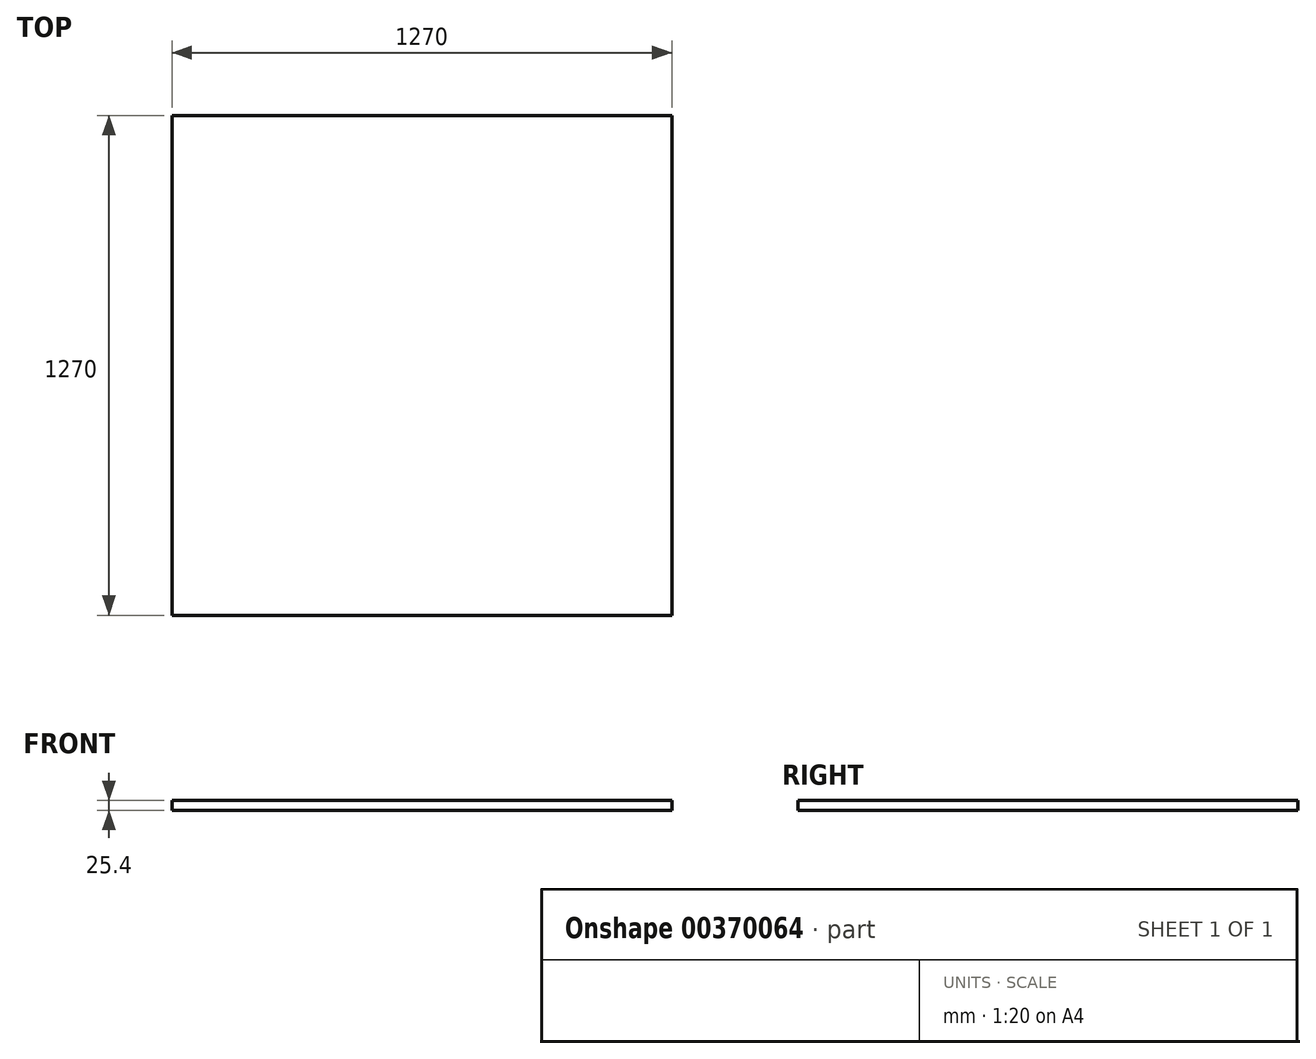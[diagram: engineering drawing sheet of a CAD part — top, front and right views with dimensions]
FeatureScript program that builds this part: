
annotation { "Feature Type Name" : "Feature", "Feature Type Description" : "" }
export const myFeature = defineFeature(function(context is Context, id is Id, definition is map)
    precondition{}
    {
        {
            var Q0;
            Q0=qCreatedBy(makeId("Top.planeOp"),FACE);
            var sketch = newSketch(context, id + "F0", { "sketchPlane" : qUnion([Q0])});
            skLineSegment(sketch, "E0.bottom", {"start": v(635, -302.65) * mm, "end": v(-635, -302.65) * mm});
            skLineSegment(sketch, "E0.top", {"start": v(635, 967.35) * mm, "end": v(-635, 967.35) * mm});
            skLineSegment(sketch, "E0.left", {"start": v(635, -302.65) * mm, "end": v(635, 967.35) * mm});
            skLineSegment(sketch, "E0.right", {"start": v(-635, -302.65) * mm, "end": v(-635, 967.35) * mm});
            skPoint(sketch, "E0.middle", {"position": v(0, 332.35) * mm});
            skLineSegment(sketch, "E1.bottom", {"start": v(-635, 256.77) * mm, "end": v(-635, 256.77) * mm});
            skLineSegment(sketch, "E1.top", {"start": v(-635, 407.93) * mm, "end": v(-635, 407.93) * mm});
            skLineSegment(sketch, "E1.left", {"start": v(-635, 256.77) * mm, "end": v(-635, 407.93) * mm});
            skLineSegment(sketch, "E1.right", {"start": v(-635, 256.77) * mm, "end": v(-635, 407.93) * mm});
            skPoint(sketch, "E1.middle", {"position": v(-635, 332.35) * mm});
            skSolve(sketch);
        }
        {
            var Q0;
            Q0 = qSketchRegion(id + "F0", true);
            extrude(context, id + "F1", {"entities" : qUnion([Q0]), "depth" : 25.4 * mm});
        }
    });
